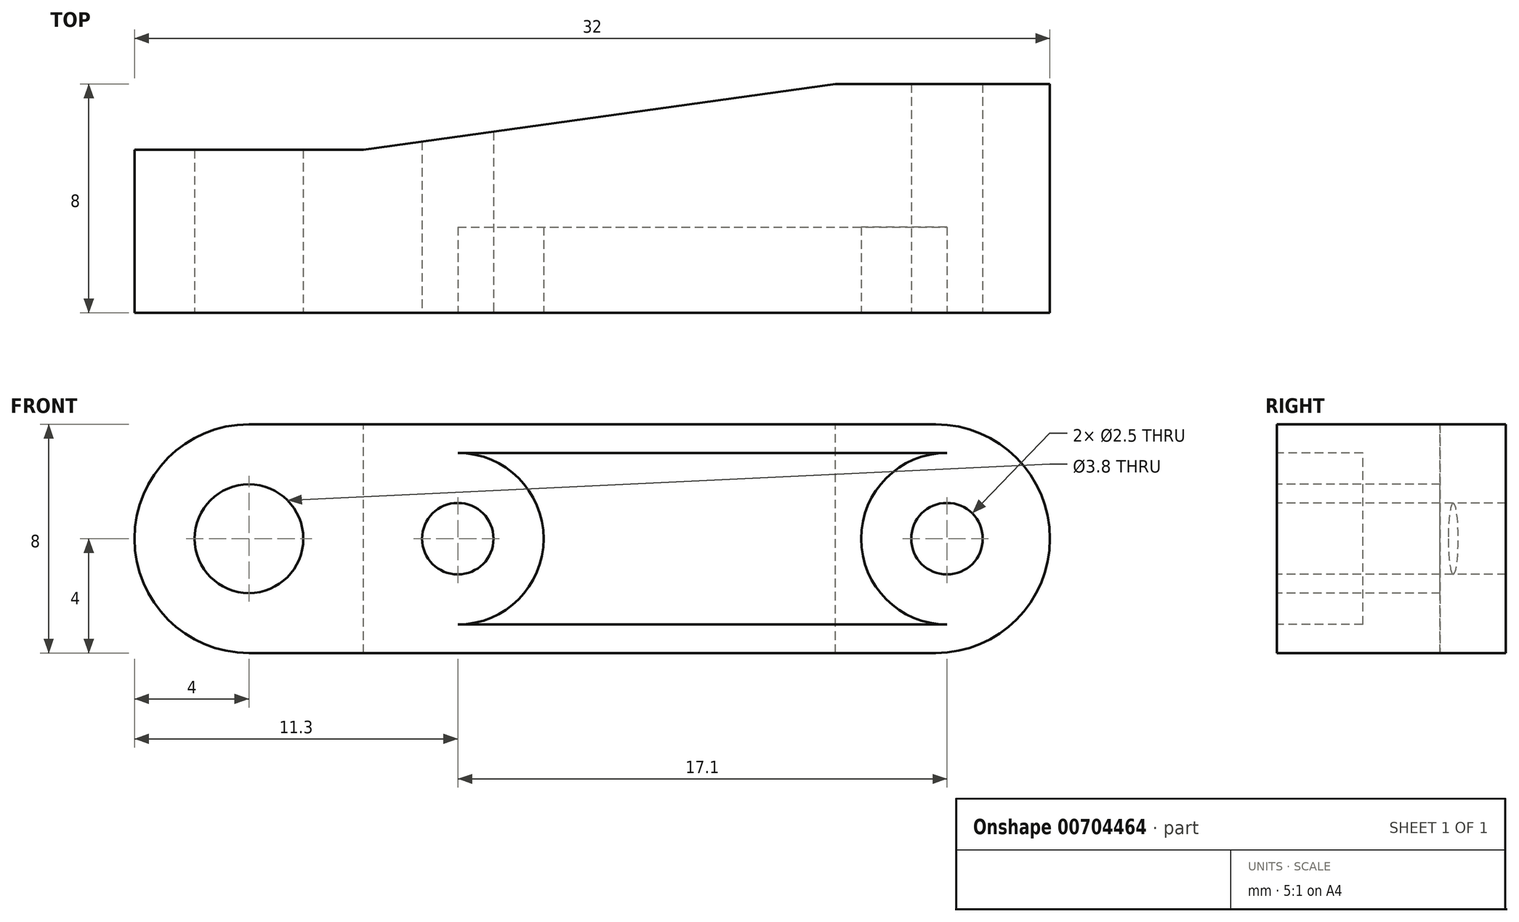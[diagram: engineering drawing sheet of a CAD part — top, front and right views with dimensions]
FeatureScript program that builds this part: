
annotation { "Feature Type Name" : "Feature", "Feature Type Description" : "" }
export const myFeature = defineFeature(function(context is Context, id is Id, definition is map)
    precondition{}
    {
        {
            var Q0;
            Q0=qCreatedBy(makeId("Front.planeOp"),FACE);
            var sketch = newSketch(context, id + "F0", { "sketchPlane" : qUnion([Q0])});
            skLineSegment(sketch, "E0.bottom", {"start": v(4, 0) * mm, "end": v(28, 0) * mm});
            skLineSegment(sketch, "E0.top", {"start": v(4, 8) * mm, "end": v(28, 8) * mm});
            skLineSegment(sketch, "E0.left", {"start": v(0, 4) * mm, "end": v(0, 4) * mm});
            skLineSegment(sketch, "E0.right", {"start": v(32, 4) * mm, "end": v(32, 4) * mm});
            skPoint(sketch, "E1.visualSharp", {"position": v(0, 8) * mm});
            skArc(sketch, "E1.filletArc", {"start": v(4, 8) * mm, "mid": v(1.17, 6.83) * mm, "end": v(0, 4) * mm});
            skPoint(sketch, "E2.visualSharp", {"position": v(0, 0) * mm});
            skArc(sketch, "E2.filletArc", {"start": v(0, 4) * mm, "mid": v(1.17, 1.17) * mm, "end": v(4, 0) * mm});
            skPoint(sketch, "E3.visualSharp", {"position": v(32, 0) * mm});
            skArc(sketch, "E3.filletArc", {"start": v(28, 0) * mm, "mid": v(30.83, 1.17) * mm, "end": v(32, 4) * mm});
            skPoint(sketch, "E4.visualSharp", {"position": v(32, 8) * mm});
            skArc(sketch, "E4.filletArc", {"start": v(32, 4) * mm, "mid": v(30.83, 6.83) * mm, "end": v(28, 8) * mm});
            skSolve(sketch);
        }
        {
            var Q0;
            Q0=makeQuery(id+"F0.imprint","IMPRINT",FACE,{"disambiguationData":[TD([[makeQuery(id+"F0.imprint","IMPRINT",EDGE,{"derivedFrom":sQuery(id+"F0.wireOp",EDGE,"E0.bottom")}),1.0]])]});
            extrude(context, id + "F1", {"entities" : qUnion([Q0]), "oppositeDirection" : true, "depth" : 8 * mm, "offsetDistance" : 25 * mm});
        }
        {
            var Q0;
            Q0=makeQuery(id+"F1.opExtrude","CAP_FACE",FACE,{"disambiguationData":[OSD([sQuery(id+"F0.wireOp",EDGE,"E0.bottom"),sQuery(id+"F0.wireOp",EDGE,"E0.top"),sQuery(id+"F0.wireOp",EDGE,"E0.left"),sQuery(id+"F0.wireOp",EDGE,"E0.right"),sQuery(id+"F0.wireOp",EDGE,"E1.filletArc"),sQuery(id+"F0.wireOp",EDGE,"E2.filletArc"),sQuery(id+"F0.wireOp",EDGE,"E3.filletArc"),sQuery(id+"F0.wireOp",EDGE,"E4.filletArc")])],"isStart":true});
            var sketch = newSketch(context, id + "F2", { "sketchPlane" : qUnion([Q0])});
            skCircle(sketch, "E5", {"center": v(4, 4) * mm, "radius": 1.9 * mm});
            skCircle(sketch, "E6", {"center": v(28.4, 4) * mm, "radius": 1.25 * mm});
            skLineSegment(sketch, "E7", {"start": v(0, 4) * mm, "end": v(32, 4) * mm, "construction": true});
            skCircle(sketch, "E8", {"center": v(11.3, 4) * mm, "radius": 1.25 * mm});
            skSolve(sketch);
        }
        {
            var Q0;
            Q0=makeQuery(id+"F2.imprint","IMPRINT",FACE,{"disambiguationData":[TD([[makeQuery(id+"F2.imprint","IMPRINT",EDGE,{"derivedFrom":sQuery(id+"F2.wireOp",EDGE,"E5")}),1.0]])]});
            var Q1;
            Q1=makeQuery(id+"F2.imprint","IMPRINT",FACE,{"disambiguationData":[TD([[makeQuery(id+"F2.imprint","IMPRINT",EDGE,{"derivedFrom":sQuery(id+"F2.wireOp",EDGE,"E8")}),1.0]])]});
            var Q2;
            Q2=makeQuery(id+"F2.imprint","IMPRINT",FACE,{"disambiguationData":[TD([[makeQuery(id+"F2.imprint","IMPRINT",EDGE,{"derivedFrom":sQuery(id+"F2.wireOp",EDGE,"E6")}),1.0]])]});
            extrude(context, id + "F3", {"entities" : qUnion([Q0, Q1, Q2]), "operationType" : NewBodyOperationType.REMOVE, "oppositeDirection" : true, "depth" : 25 * mm, "offsetDistance" : 25 * mm});
        }
        {
            var Q0;
            Q0=makeQuery(id+"F1.opExtrude","SWEPT_FACE",FACE,{"disambiguationData":[OSD([sQuery(id+"F0.wireOp",EDGE,"E0.top")])]});
            var sketch = newSketch(context, id + "F4", { "sketchPlane" : qUnion([Q0])});
            skLineSegment(sketch, "E9", {"start": v(0, 5.7) * mm, "end": v(8, 5.7) * mm});
            skLineSegment(sketch, "E10", {"start": v(8, 5.7) * mm, "end": v(24.5, 8) * mm});
            skLineSegment(sketch, "E11", {"start": v(24.5, 8) * mm, "end": v(0, 8) * mm});
            skLineSegment(sketch, "E12", {"start": v(0, 8) * mm, "end": v(0, 5.7) * mm});
            skLineSegment(sketch, "E13", {"start": v(32, 8) * mm, "end": v(32, 0) * mm, "construction": true});
            skSolve(sketch);
        }
        {
            var Q0;
            {var subQ0=sQuery(id+"F4.wireOp",EDGE,"E10");Q0=makeQuery(id+"F4.imprint","IMPRINT",FACE,{"disambiguationData":[TD([[makeQuery(id+"F4.imprint","IMPRINT",EDGE,{"derivedFrom":subQ0}),1.0]])]});}
            var Q1;
            {var subQ0=sQuery(id+"F4.wireOp",EDGE,"E12");Q1=makeQuery(id+"F4.imprint","IMPRINT",FACE,{"disambiguationData":[TD([[makeQuery(id+"F4.imprint","IMPRINT",EDGE,{"derivedFrom":subQ0}),1.0]])]});}
            extrude(context, id + "F5", {"entities" : qUnion([Q0, Q1]), "operationType" : NewBodyOperationType.REMOVE, "oppositeDirection" : true, "depth" : 25 * mm, "offsetDistance" : 25 * mm});
        }
        {
            var Q0;
            Q0=makeQuery(id+"F1.opExtrude","CAP_FACE",FACE,{"disambiguationData":[OSD([sQuery(id+"F0.wireOp",EDGE,"E0.bottom"),sQuery(id+"F0.wireOp",EDGE,"E0.top"),sQuery(id+"F0.wireOp",EDGE,"E1.filletArc"),sQuery(id+"F0.wireOp",EDGE,"E2.filletArc"),sQuery(id+"F0.wireOp",EDGE,"E3.filletArc"),sQuery(id+"F0.wireOp",EDGE,"E4.filletArc")])],"isStart":true});
            var sketch = newSketch(context, id + "F6", { "sketchPlane" : qUnion([Q0])});
            skArc(sketch, "E14", {"start": v(11.3, 1) * mm, "mid": v(14.3, 4) * mm, "end": v(11.3, 7) * mm});
            skArc(sketch, "E15", {"start": v(28.4, 7) * mm, "mid": v(25.4, 4) * mm, "end": v(28.4, 1) * mm});
            skLineSegment(sketch, "E16", {"start": v(11.3, 7) * mm, "end": v(28.4, 7) * mm});
            skLineSegment(sketch, "E17", {"start": v(11.3, 1) * mm, "end": v(28.4, 1) * mm});
            skSolve(sketch);
        }
        {
            var Q0;
            Q0=makeQuery(id+"F6.imprint","IMPRINT",FACE,{"disambiguationData":[TD([[makeQuery(id+"F6.imprint","IMPRINT",EDGE,{"derivedFrom":sQuery(id+"F6.wireOp",EDGE,"E14")}),-1.0]])]});
            extrude(context, id + "F7", {"entities" : qUnion([Q0]), "operationType" : NewBodyOperationType.REMOVE, "oppositeDirection" : true, "depth" : 3 * mm, "offsetDistance" : 25 * mm});
        }
    });
